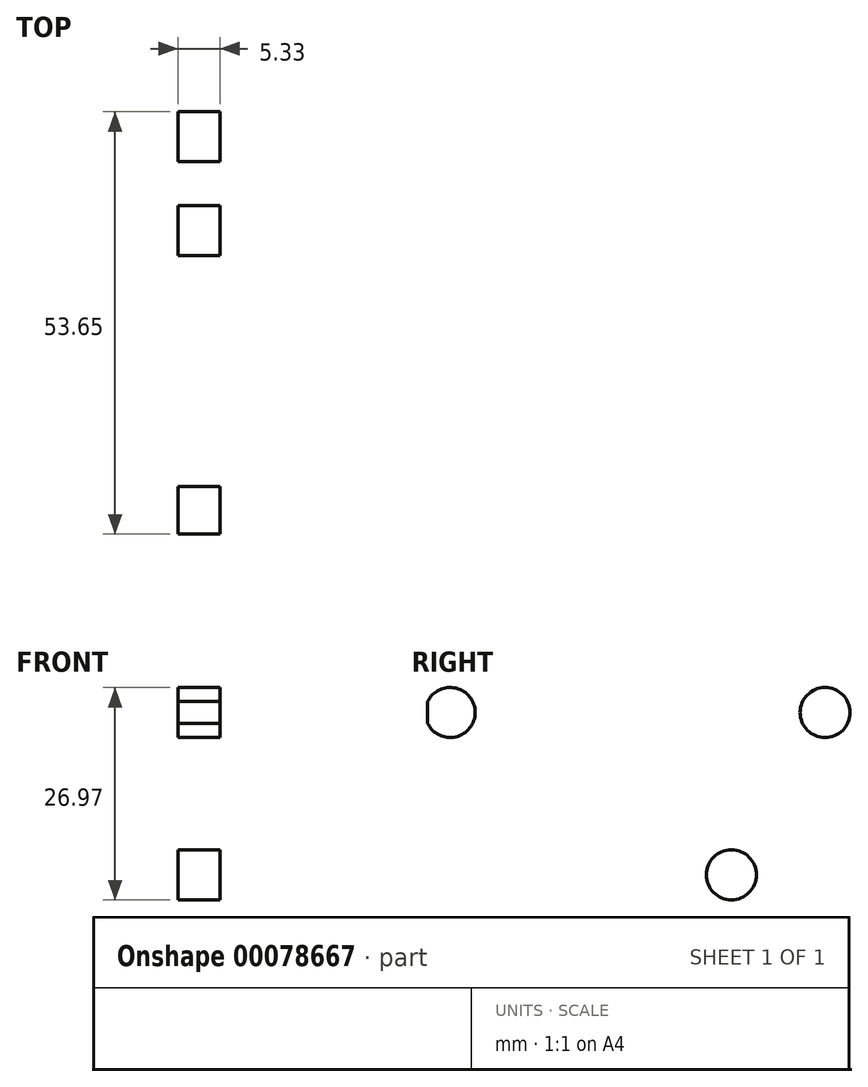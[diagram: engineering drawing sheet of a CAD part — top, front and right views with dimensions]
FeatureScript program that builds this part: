
annotation { "Feature Type Name" : "Feature", "Feature Type Description" : "" }
export const myFeature = defineFeature(function(context is Context, id is Id, definition is map)
    precondition{}
    {
        {
            var Q0;
            Q0=qCreatedBy(makeId("Right.planeOp"),FACE);
            var sketch = newSketch(context, id + "F0", { "sketchPlane" : qUnion([Q0])});
            skLineSegment(sketch, "E0.bottom", {"start": v(-239.83, -75.22) * mm, "end": v(115.77, -75.22) * mm});
            skLineSegment(sketch, "E0.top", {"start": v(-239.83, -126.02) * mm, "end": v(115.77, -126.02) * mm});
            skLineSegment(sketch, "E0.left", {"start": v(-239.83, -75.22) * mm, "end": v(-239.83, -126.02) * mm});
            skLineSegment(sketch, "E0.right", {"start": v(115.77, -75.22) * mm, "end": v(115.77, -126.02) * mm});
            skCircle(sketch, "E1", {"center": v(-213.17, -100.62) * mm, "radius": 6.35 * mm});
            skPoint(sketch, "E1.centerSnap0", {"position": v(-239.83, -100.62) * mm});
            skCircle(sketch, "E2", {"center": v(90.37, -100.62) * mm, "radius": 6.35 * mm});
            skPoint(sketch, "E2.centerSnap0", {"position": v(115.77, -100.62) * mm});
            skSolve(sketch);
        }
        {
            var Q0;
            Q0=makeQuery(id+"F0.imprint","IMPRINT",FACE,{"disambiguationData":[TD([[makeQuery(id+"F0.imprint","IMPRINT",EDGE,{"derivedFrom":sQuery(id+"F0.wireOp",EDGE,"E0.top")}),1.0]])]});
            extrude(context, id + "F1", {"entities" : qUnion([Q0]), "depth" : 5.33 * mm});
        }
        {
            var Q0;
            Q0=makeQuery(id+"F1.opExtrude","SWEPT_EDGE",EDGE,{"disambiguationData":[OSD([sQuery(id+"F0.wireOp",EDGE,"E0.top"),sQuery(id+"F0.wireOp",EDGE,"E0.right"),sQuery(id+"F0.wireOp",EDGE,"YhQDp708-v9PV-gCd5-4eMr-qxxqGINb4CNa")])]});
            var Q1;
            Q1=makeQuery(id+"F1.opExtrude","SWEPT_EDGE",EDGE,{"disambiguationData":[OSD([sQuery(id+"F0.wireOp",EDGE,"E0.bottom"),sQuery(id+"F0.wireOp",EDGE,"JfkSez95-TpPm-lS6h-l0PS-dWdjHvY3Lj4y")])]});
            fillet(context, id + "F2", {"entities" : qUnion([Q0, Q1]), "radius" : 2.54 * mm, "tangentPropagation" : true, "allowEdgeOverflow" : false});
        }
        {
            var Q0;
            Q0=makeQuery(id+"F1.opExtrude","CAP_FACE",FACE,{"disambiguationData":[OSD([sQuery(id+"F0.wireOp",EDGE,"E0.bottom"),sQuery(id+"F0.wireOp",EDGE,"E0.top"),sQuery(id+"F0.wireOp",EDGE,"E0.left"),sQuery(id+"F0.wireOp",EDGE,"E1"),sQuery(id+"F0.wireOp",EDGE,"YhQDp708-v9PV-gCd5-4eMr-qxxqGINb4CNa"),sQuery(id+"F0.wireOp",EDGE,"JfkSez95-TpPm-lS6h-l0PS-dWdjHvY3Lj4y"),sQuery(id+"F0.wireOp",EDGE,"8f25c41c-40bb-4eb7-89e6-922f386cb548.filletArc")])],"isStart":false});
            var sketch = newSketch(context, id + "F3", { "sketchPlane" : qUnion([Q0])});
            skCircle(sketch, "E3", {"center": v(-213.17, -100.62) * mm, "radius": 23.81 * mm});
            skCircle(sketch, "E4", {"center": v(-189.36, -100.62) * mm, "radius": 3.18 * mm});
            skCircle(sketch, "E5.1.0", {"center": v(-201.26, -80) * mm, "radius": 3.18 * mm});
            skCircle(sketch, "E5.2.0", {"center": v(-225.07, -80) * mm, "radius": 3.18 * mm});
            skCircle(sketch, "E5.3.0", {"center": v(-236.98, -100.62) * mm, "radius": 3.18 * mm});
            skCircle(sketch, "E5.4.0", {"center": v(-225.07, -121.24) * mm, "radius": 3.18 * mm});
            skCircle(sketch, "E5.5.0", {"center": v(-201.26, -121.24) * mm, "radius": 3.18 * mm});
            skSolve(sketch);
        }
        {
            var Q0;
            {var subQ0=sQuery(id+"F3.wireOp",EDGE,"E5.1.0");var subQ1=sQuery(id+"F3.wireOp",EDGE,"E3");var subQ2=makeQuery(id+"F3.imprint","INTERSECT",VERTEX,{"disambiguationData":[OD(0.0)],"derivedFrom":[subQ1,subQ0]});Q0=makeQuery(id+"F3.imprint","IMPRINT",FACE,{"disambiguationData":[TD([[makeQuery(id+"F3.imprint","IMPRINT",EDGE,{"disambiguationData":[TD([[subQ2,-1.0]])],"derivedFrom":subQ1}),-1.0]])]});}
            var Q1;
            {var subQ0=sQuery(id+"F3.wireOp",EDGE,"E5.2.0");var subQ1=sQuery(id+"F3.wireOp",EDGE,"E3");var subQ2=makeQuery(id+"F3.imprint","INTERSECT",VERTEX,{"disambiguationData":[OD(0.0)],"derivedFrom":[subQ1,subQ0]});Q1=makeQuery(id+"F3.imprint","IMPRINT",FACE,{"disambiguationData":[TD([[makeQuery(id+"F3.imprint","IMPRINT",EDGE,{"disambiguationData":[TD([[subQ2,-1.0]])],"derivedFrom":subQ1}),-1.0]])]});}
            var Q2;
            {var subQ0=sQuery(id+"F3.wireOp",EDGE,"E5.2.0");var subQ1=sQuery(id+"F3.wireOp",EDGE,"E3");var subQ2=makeQuery(id+"F3.imprint","INTERSECT",VERTEX,{"disambiguationData":[OD(0.0)],"derivedFrom":[subQ1,subQ0]});Q2=makeQuery(id+"F3.imprint","IMPRINT",FACE,{"disambiguationData":[TD([[makeQuery(id+"F3.imprint","IMPRINT",EDGE,{"disambiguationData":[TD([[subQ2,-1.0]])],"derivedFrom":subQ1}),1.0]])]});}
            var Q3;
            {var subQ0=sQuery(id+"F3.wireOp",EDGE,"E5.1.0");var subQ1=sQuery(id+"F3.wireOp",EDGE,"E3");var subQ2=makeQuery(id+"F3.imprint","INTERSECT",VERTEX,{"disambiguationData":[OD(0.0)],"derivedFrom":[subQ1,subQ0]});Q3=makeQuery(id+"F3.imprint","IMPRINT",FACE,{"disambiguationData":[TD([[makeQuery(id+"F3.imprint","IMPRINT",EDGE,{"disambiguationData":[TD([[subQ2,-1.0]])],"derivedFrom":subQ1}),1.0]])]});}
            var Q4;
            {var subQ0=sQuery(id+"F3.wireOp",EDGE,"E4");var subQ1=sQuery(id+"F3.wireOp",EDGE,"E3");var subQ2=makeQuery(id+"F3.imprint","INTERSECT",VERTEX,{"disambiguationData":[OD(0.0)],"derivedFrom":[subQ1,subQ0]});Q4=makeQuery(id+"F3.imprint","IMPRINT",FACE,{"disambiguationData":[TD([[makeQuery(id+"F3.imprint","IMPRINT",EDGE,{"disambiguationData":[TD([[subQ2,1.0]])],"derivedFrom":subQ1}),1.0]])]});}
            var Q5;
            {var subQ0=sQuery(id+"F3.wireOp",EDGE,"E4");var subQ1=sQuery(id+"F3.wireOp",EDGE,"E3");var subQ2=makeQuery(id+"F3.imprint","INTERSECT",VERTEX,{"disambiguationData":[OD(0.0)],"derivedFrom":[subQ1,subQ0]});Q5=makeQuery(id+"F3.imprint","IMPRINT",FACE,{"disambiguationData":[TD([[makeQuery(id+"F3.imprint","IMPRINT",EDGE,{"disambiguationData":[TD([[subQ2,1.0]])],"derivedFrom":subQ1}),-1.0]])]});}
            var Q6;
            {var subQ0=sQuery(id+"F3.wireOp",EDGE,"E5.5.0");var subQ1=sQuery(id+"F3.wireOp",EDGE,"E3");var subQ2=makeQuery(id+"F3.imprint","INTERSECT",VERTEX,{"disambiguationData":[OD(0.0)],"derivedFrom":[subQ1,subQ0]});Q6=makeQuery(id+"F3.imprint","IMPRINT",FACE,{"disambiguationData":[TD([[makeQuery(id+"F3.imprint","IMPRINT",EDGE,{"disambiguationData":[TD([[subQ2,-1.0]])],"derivedFrom":subQ1}),-1.0]])]});}
            var Q7;
            {var subQ0=sQuery(id+"F3.wireOp",EDGE,"E5.5.0");var subQ1=sQuery(id+"F3.wireOp",EDGE,"E3");var subQ2=makeQuery(id+"F3.imprint","INTERSECT",VERTEX,{"disambiguationData":[OD(0.0)],"derivedFrom":[subQ1,subQ0]});Q7=makeQuery(id+"F3.imprint","IMPRINT",FACE,{"disambiguationData":[TD([[makeQuery(id+"F3.imprint","IMPRINT",EDGE,{"disambiguationData":[TD([[subQ2,-1.0]])],"derivedFrom":subQ1}),1.0]])]});}
            var Q8;
            {var subQ0=sQuery(id+"F3.wireOp",EDGE,"E5.4.0");var subQ1=sQuery(id+"F3.wireOp",EDGE,"E3");var subQ2=makeQuery(id+"F3.imprint","INTERSECT",VERTEX,{"disambiguationData":[OD(0.0)],"derivedFrom":[subQ1,subQ0]});Q8=makeQuery(id+"F3.imprint","IMPRINT",FACE,{"disambiguationData":[TD([[makeQuery(id+"F3.imprint","IMPRINT",EDGE,{"disambiguationData":[TD([[subQ2,-1.0]])],"derivedFrom":subQ1}),-1.0]])]});}
            var Q9;
            {var subQ0=sQuery(id+"F3.wireOp",EDGE,"E5.4.0");var subQ1=sQuery(id+"F3.wireOp",EDGE,"E3");var subQ2=makeQuery(id+"F3.imprint","INTERSECT",VERTEX,{"disambiguationData":[OD(0.0)],"derivedFrom":[subQ1,subQ0]});Q9=makeQuery(id+"F3.imprint","IMPRINT",FACE,{"disambiguationData":[TD([[makeQuery(id+"F3.imprint","IMPRINT",EDGE,{"disambiguationData":[TD([[subQ2,-1.0]])],"derivedFrom":subQ1}),1.0]])]});}
            extrude(context, id + "F4", {"entities" : qUnion([Q0, Q1, Q2, Q3, Q4, Q5, Q6, Q7, Q8, Q9]), "operationType" : NewBodyOperationType.REMOVE, "oppositeDirection" : true, "depth" : 25.4 * mm});
        }
    });
